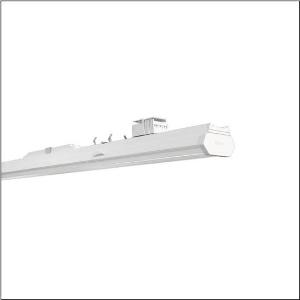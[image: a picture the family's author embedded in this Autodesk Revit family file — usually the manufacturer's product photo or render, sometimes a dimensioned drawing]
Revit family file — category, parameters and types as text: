
# Revit family: licross_r__11_protected_mo_51tp12dn695g_2e2e
name_source: partatom
category: Lighting Fixtures
units: mm (PartAtom-declared; Revit-internal decimal feet)

## family parameters
Cut with Voids When Loaded = No
Host = Face
Light Source = No
Part Type = Normal
Room Calculation Point = No
Round Connector Dimension = Use Diameter
Shared = No

## types (1)
- --- (1 x LED, 9730 lm, 57.1 W, 6500K)
    Apparent Load = 57 VA
    CIE Flux Codes = 73 92 98 99 100
    Color Rendering = 80
    Color Temperature = 6500K
    Default Elevation = 1800 mm
    Description = Licross® 11 Protected MO, luminaire insert, of sheet steel, galvanised, coil coated, white, length: 1.500mm, width: 90mm, height: 101mm, LED rated luminous flux: 9.730lm, light colour: 865, control gear: DALI 2, with plug, 5-pole, with phase selection, mains connection: 220..240V, AC, 50/60Hz, rated input power: 57W, halogen-free wiring, primary optical cover: cover, of PMMA, light emission: direct distribution, primary light characteristic: symmetric, protection rating (complete): IP64, insulation class (complete): insulation class I (protective earthing), certification: CE, ENEC, VDE, UKCA, protection symbol: D if used in an environment with conductive dust loads with corresponding accessories, impact resistance: IK06, permissible ambient temperature for indoor applications: -25..+35°C, corresponds to IFS (International Featured Standards) requirements for safety and quality in the food industry, reducing of maximum allowable ambient temperature of 5°C with ceiling mounting, LABS conformity tested according to VDMA 24364:2018-05, packaging unit: 1 piece
    Height = 92 mm
    Lamp = 1 x LED
    Lamp Light Flux = 9730 lm
    Lamp Power = 57.1 W
    Lamp count = 1
    Length = 1500 mm
    Luminous efficacy = 170 lm/W
    Manufacturer = Siteco
    ModVariant = No
    Model = 51TP12DN695G
    Mounting Place = Ceiling
    Mounting Type = Pendant
    Number of Poles = 1
    OnlyDefault = Yes
    Power Factor = 1
    Product Name = Licross® 11 Protected MO
    Product group = luminaire insert
    ProductGroupID = 901
    Protection Class = Protection class I
    Protection Degree = IP 64
    RLX_Detail_Level = 1
    RLX_Emergency_Light_Flux = 0 lm
    RLX_Emergency_Type = 0
    RLX_Emergency_Type_DB = No
    RlxData = <blob elided: 24325 chars, md5=c9165e02>
    Socket = socket
    Standby Power = 0 W
    System Light Flux = 9730 lm
    System Power = 57 W
    Type Comments = factory setting: luminous flux: 100 % | dim-lin: 254 | 378 mA
    Type Image = l_1256148.jpg
    URL = http://relux.com
    VarID = @adj_046585
    Voltage = 0 V
    Weight = 0.00 kg
    Width = 88 mm

## geometry (parser evidence)
native form markers: Blend x4, Sweep x9
no freeform markers — native parametric forms only
